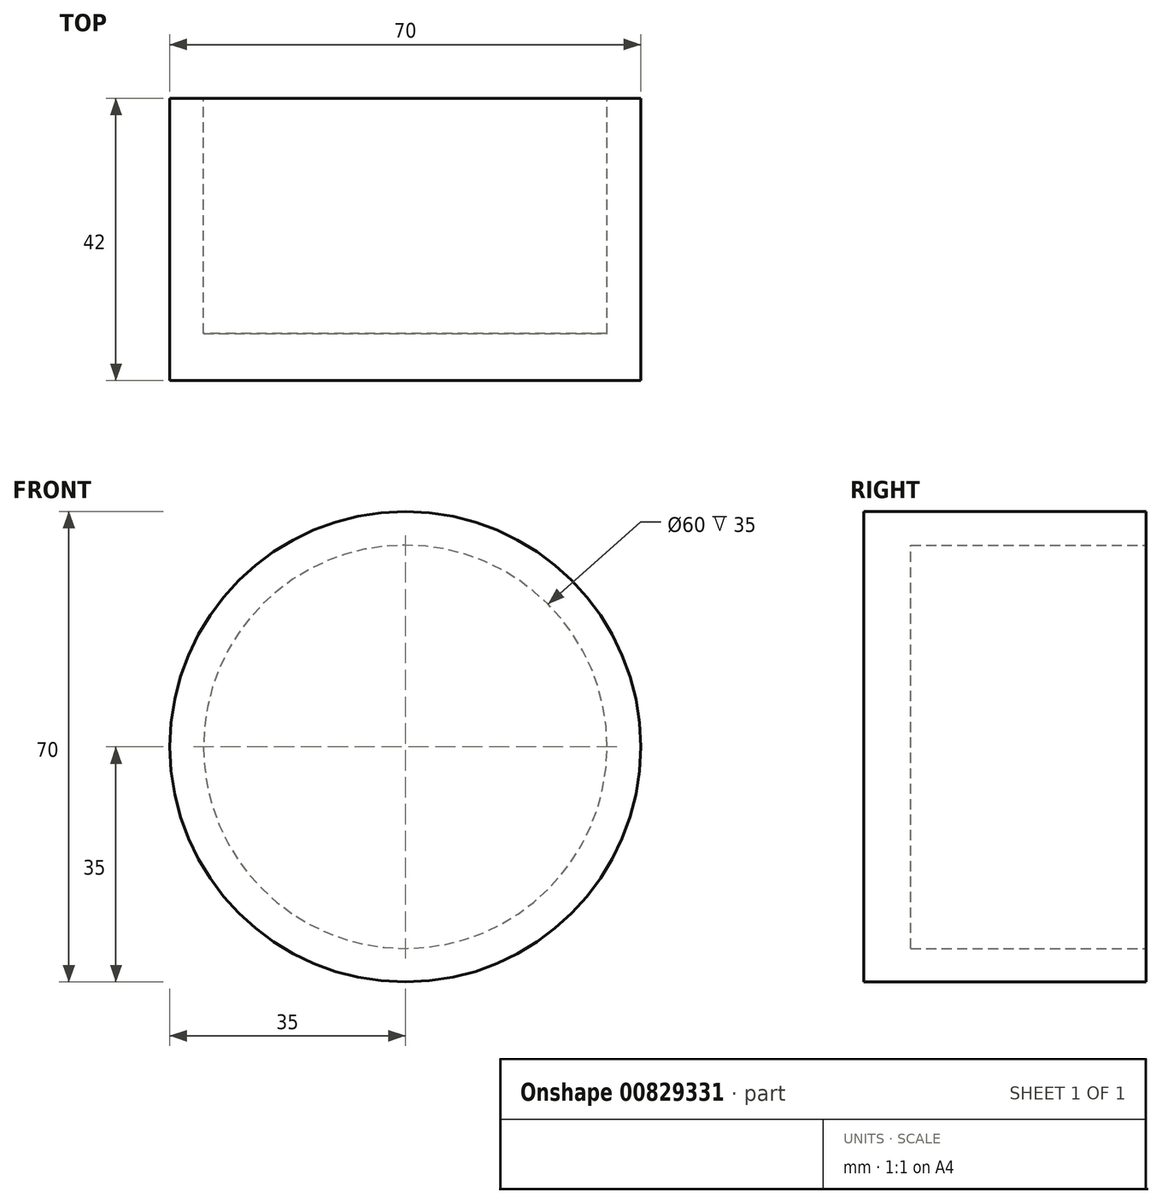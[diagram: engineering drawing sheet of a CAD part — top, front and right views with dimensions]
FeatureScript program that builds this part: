
annotation { "Feature Type Name" : "Feature", "Feature Type Description" : "" }
export const myFeature = defineFeature(function(context is Context, id is Id, definition is map)
    precondition{}
    {
        {
            var Q0;
            Q0=qCreatedBy(makeId("Front.planeOp"),FACE);
            var sketch = newSketch(context, id + "F0", { "sketchPlane" : qUnion([Q0])});
            skCircle(sketch, "E0", {"center": v(0, 0) * mm, "radius": 30 * mm});
            skCircle(sketch, "E1", {"center": v(0, 0) * mm, "radius": 35 * mm});
            skSolve(sketch);
        }
        {
            var Q0;
            Q0=makeQuery(id+"F0.imprint","IMPRINT",FACE,{"disambiguationData":[TD([[makeQuery(id+"F0.imprint","IMPRINT",EDGE,{"derivedFrom":sQuery(id+"F0.wireOp",EDGE,"E0")}),-1.0]])]});
            extrude(context, id + "F1", {"entities" : qUnion([Q0]), "depth" : 35 * mm, "offsetDistance" : 25 * mm});
        }
        {
            var Q0;
            Q0=makeQuery(id+"F1.opExtrude","CAP_FACE",FACE,{"disambiguationData":[OSD([sQuery(id+"F0.wireOp",EDGE,"E0"),sQuery(id+"F0.wireOp",EDGE,"E1")])],"isStart":false});
            var sketch = newSketch(context, id + "F2", { "sketchPlane" : qUnion([Q0])});
            skCircle(sketch, "E2", {"center": v(0, 0) * mm, "radius": 35 * mm});
            skSolve(sketch);
        }
        {
            var Q0;
            Q0=qSketchRegion(id+"F2",true);
            extrude(context, id + "F3", {"entities" : qUnion([Q0]), "operationType" : NewBodyOperationType.ADD, "depth" : 7 * mm, "offsetDistance" : 25 * mm});
        }
    });
